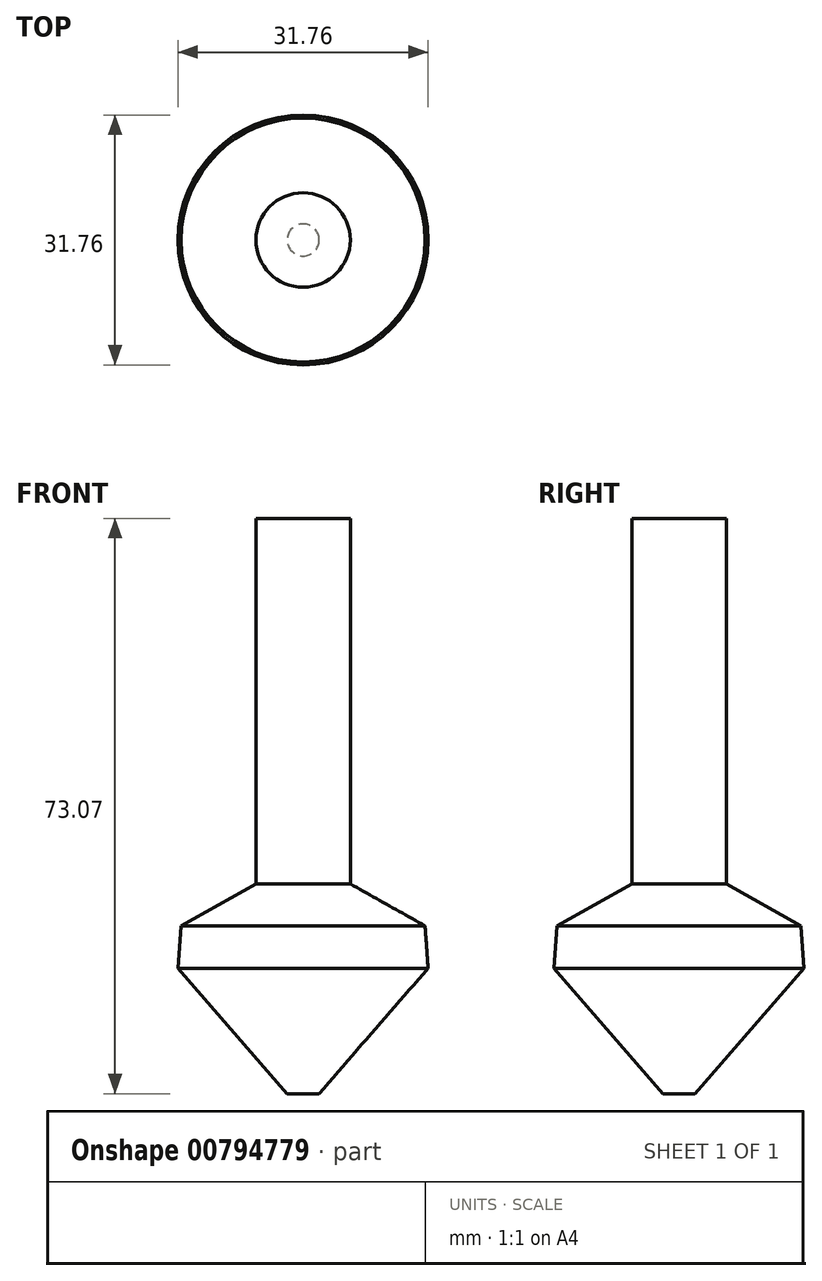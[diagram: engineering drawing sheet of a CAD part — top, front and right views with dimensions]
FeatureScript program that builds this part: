
annotation { "Feature Type Name" : "Feature", "Feature Type Description" : "" }
export const myFeature = defineFeature(function(context is Context, id is Id, definition is map)
    precondition{}
    {
        {
            var Q0;
            Q0=qCreatedBy(makeId("Front.planeOp"),FACE);
            var sketch = newSketch(context, id + "F0", { "sketchPlane" : qUnion([Q0])});
            skLineSegment(sketch, "E0", {"start": v(0, 0) * mm, "end": v(2.03, 0) * mm});
            skLineSegment(sketch, "E1", {"start": v(2.03, 0) * mm, "end": v(15.88, 15.92) * mm});
            skLineSegment(sketch, "E2", {"start": v(15.88, 15.92) * mm, "end": v(15.5, 21.3) * mm});
            skLineSegment(sketch, "E3", {"start": v(15.5, 21.3) * mm, "end": v(6, 26.64) * mm});
            skLineSegment(sketch, "E4", {"start": v(6, 26.64) * mm, "end": v(6, 73.07) * mm});
            skLineSegment(sketch, "E5", {"start": v(6, 73.07) * mm, "end": v(0, 73.07) * mm});
            skLineSegment(sketch, "E6", {"start": v(0, 73.07) * mm, "end": v(0, 0) * mm});
            skSolve(sketch);
        }
        {
            var Q0;
            Q0=qSketchRegion(id+"F0",true);
            var Q1;
            Q1=sQuery(id+"F0.wireOp",EDGE,"E6");
            revolve(context, id + "F1", {"surfaceOperationType" : NewSurfaceOperationType.NEW, "entities" : qUnion([Q0]), "axis" : qUnion([Q1]), "revolveType" : RevolveType.FULL});
        }
    });
